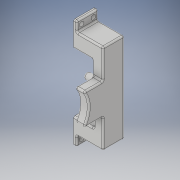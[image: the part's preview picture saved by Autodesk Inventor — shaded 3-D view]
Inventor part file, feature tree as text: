
AUTODESK INVENTOR PART (.ipt)
format: ipt  version: 2018 (Build 220112000, 112)  size: 376,320 bytes
history: native  units: in
note: dims shown in document units (in); Inventor stores cm internally (conversion verified against a paired STEP export)
features: reference x23, sketch x13, extrude x12, other x9, fillet x5, projected_geometry x3
ambient origin geometry x8: Origin, YZ Plane, XZ Plane, XY Plane, X Axis, Y Axis, Z Axis, Center Point
bodies: Solid1 (feature_tree)
feature tree (65):
  extrude  "Extrusion1"  Depth=0.5in
  extrude  "Extrusion2"  Depth=0.4724in TaperAngle=0.0deg
  sketch  "Sketch3"  dims[d5=0.0787in d6=0.0in d7=0.2in d8=0.0in]
  extrude  "Extrusion3"  Depth=0.0787in TaperAngle=0.0deg
  extrude  "Extrusion4"  Depth=0.4in
  extrude  "Extrusion5"  Depth=0.25in
  extrude  "Extrusion6"  Depth=0.0787in TaperAngle=0.0deg
  extrude  "Extrusion7"  Depth=0.1181in
  extrude  "Extrusion8"  Depth=0.1181in
  extrude  "Extrusion10"  Depth=0.0787in TaperAngle=0.0deg
  extrude  "Extrusion12"  Depth=0.25in TaperAngle=0.0deg
  fillet  "Fillet2"  Radius=0.75in
  fillet  "Fillet3"  Radius=0.75in
  extrude  "Extrusion13"  Depth=0.0394in
  fillet  "Fillet4"  Radius=1.0in
  fillet  "Fillet6"  Radius=0.0394in
  extrude  "Extrusion14"  Depth=0.65in
  fillet  "Fillet8"  Radius=1.0in
  sketch  "Sketch1"  dims[d0=0.5in d1=0.125in]
  reference  "Reference1"
  reference  "Reference2"
  reference  "Reference3"
  reference  "Reference4"
  reference  "Reference5"
  reference  "Reference6"
  reference  "Reference7"
  reference  "Reference8"
  reference  "Reference9"
  reference  "Reference10"
  reference  "Reference11"
  reference  "Reference12"
  reference  "Reference13"
  reference  "Reference14"
  reference  "Reference15"
  reference  "Reference16"
  reference  "Reference17"
  sketch  "Sketch2"  dims[d2=0.7in d3=0.4724in d4=0.0in]
  projected_geometry  "Projected Loop1"
  projected_geometry  "Projected Loop2"
  reference  "Reference18"
  reference  "Reference19"
  sketch  "Sketch4"  dims[d9=0.4in d10=0.4in]
  projected_geometry  "Projected Loop3"
  sketch  "Sketch5"  dims[d11=0.5512in d12=0.0in d13=0.25in]
  reference  "Reference20"
  sketch  "Sketch6"  dims[d14=0.25in d15=0.0787in d16=0.0in]
  sketch  "Sketch7"  dims[d17=0.125in d18=0.1181in]
  sketch  "Sketch8"  dims[d19=0.125in d20=0.1181in]
  reference  "Reference21"
  sketch  "Sketch9"  dims[d21=1.15in d22=0.0787in d23=0.0in]
  sketch  "Sketch11"  dims[d24=1.0in d25=0.0in d26=0.25in d27=0.0in d31=0.75in d32=0.75in]
  reference  "Reference23"
  sketch  "Sketch13"  dims[d33=0.5in d34=0.0in d38=0.1575in d39=1.0in d40=0.0in d42=0.0394in]
  reference  "Reference25"
  sketch  "Sketch14"  dims[d43=0.0394in d44=0.65in d45=1.0in d46=0.0in]
  sketch  "Sketch15"  dims[d47=0.0394in d49=0.0394in d51=0.0098in d52=0.0in d53=0.0394in]
  other  "<userpath>\OneDrive\Documents\Inventor\TSA\2018\Animatronics\Tortoise\AssemblyTURTLE.iam"
  other  "AssemblyTURTLE.iam"
  other  "servo (2):1"
  other  "smallergear:1"
  other  "Frame:1"
  other  "<userpath>\OneDrive\Documents\Inventor\TSA\2018\Animatronics\Tortoise\TurtleAssembly.iam"
  other  "TurtleAssembly.iam"
  other  "smallergear:3"
  other  "holder_gear_mount:1"
